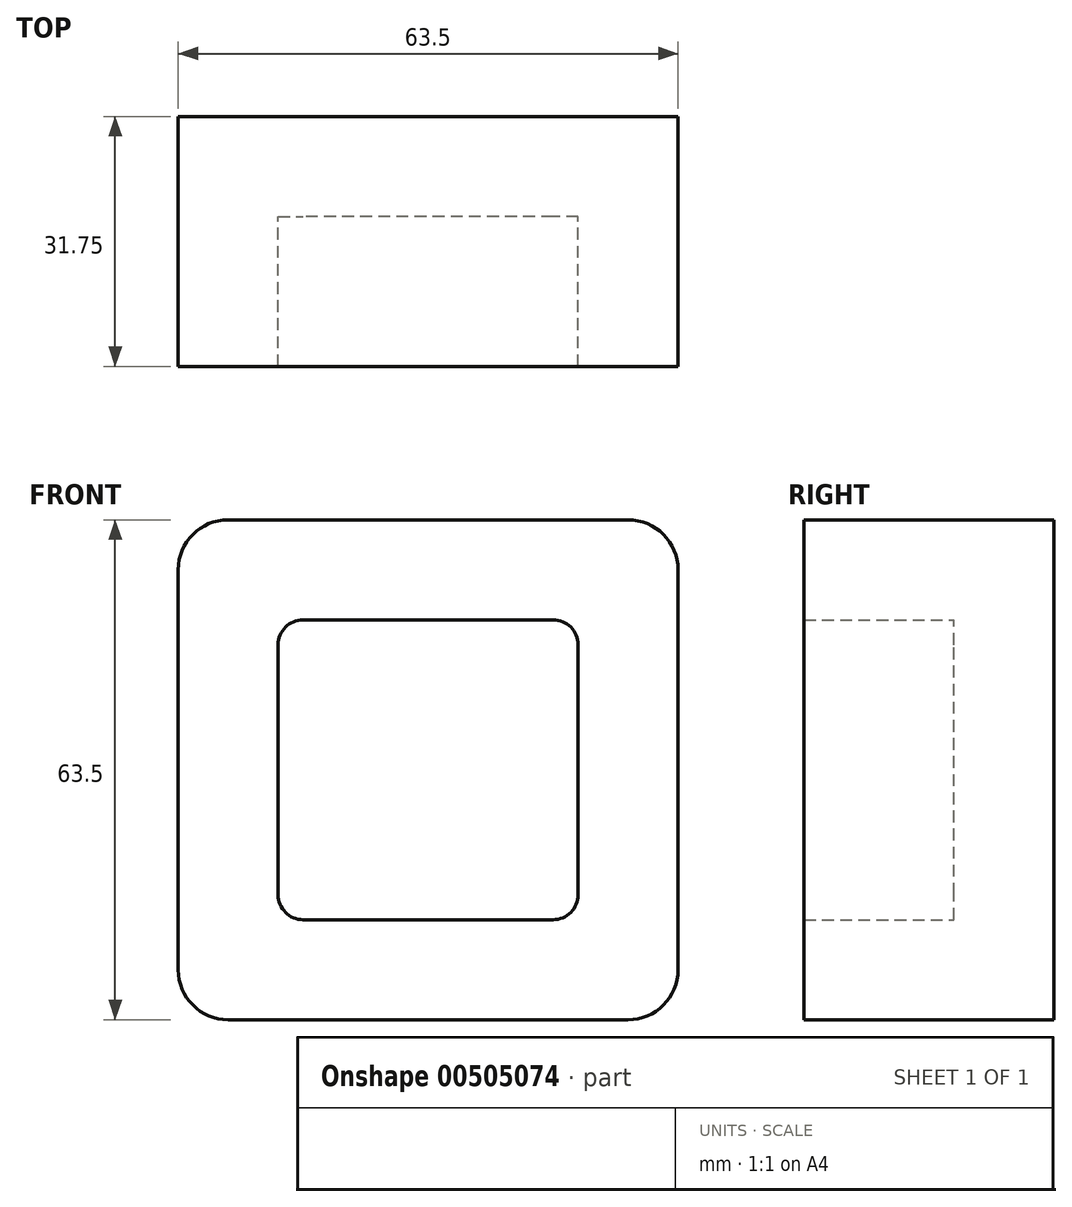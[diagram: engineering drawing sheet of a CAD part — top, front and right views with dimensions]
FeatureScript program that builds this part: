
annotation { "Feature Type Name" : "Feature", "Feature Type Description" : "" }
export const myFeature = defineFeature(function(context is Context, id is Id, definition is map)
    precondition{}
    {
        {
            var Q0;
            Q0=qCreatedBy(makeId("Front.planeOp"),FACE);
            var sketch = newSketch(context, id + "F0", { "sketchPlane" : qUnion([Q0])});
            skLineSegment(sketch, "E0.bottom", {"start": v(25.4, -31.75) * mm, "end": v(-25.4, -31.75) * mm});
            skLineSegment(sketch, "E0.top", {"start": v(25.4, 31.75) * mm, "end": v(-25.4, 31.75) * mm});
            skLineSegment(sketch, "E0.left", {"start": v(31.75, -25.4) * mm, "end": v(31.75, 25.4) * mm});
            skLineSegment(sketch, "E0.right", {"start": v(-31.75, -25.4) * mm, "end": v(-31.75, 25.4) * mm});
            skPoint(sketch, "E0.middle", {"position": v(0, 0) * mm});
            skPoint(sketch, "E1.visualSharp", {"position": v(-31.75, 31.75) * mm});
            skArc(sketch, "E1.filletArc", {"start": v(-25.4, 31.75) * mm, "mid": v(-29.9, 29.9) * mm, "end": v(-31.75, 25.4) * mm});
            skPoint(sketch, "E2.visualSharp", {"position": v(31.75, 31.75) * mm});
            skArc(sketch, "E2.filletArc", {"start": v(31.75, 25.4) * mm, "mid": v(29.9, 29.9) * mm, "end": v(25.4, 31.75) * mm});
            skPoint(sketch, "E3.visualSharp", {"position": v(31.75, -31.75) * mm});
            skArc(sketch, "E3.filletArc", {"start": v(25.4, -31.75) * mm, "mid": v(29.9, -29.9) * mm, "end": v(31.75, -25.4) * mm});
            skPoint(sketch, "E4.visualSharp", {"position": v(-31.75, -31.75) * mm});
            skArc(sketch, "E4.filletArc", {"start": v(-31.75, -25.4) * mm, "mid": v(-29.9, -29.9) * mm, "end": v(-25.4, -31.75) * mm});
            skLineSegment(sketch, "E5.0", {"start": v(-19.05, -15.87) * mm, "end": v(-19.05, 15.88) * mm});
            skLineSegment(sketch, "E5.1", {"start": v(15.87, -19.05) * mm, "end": v(-15.88, -19.05) * mm});
            skLineSegment(sketch, "E5.2", {"start": v(19.05, -15.87) * mm, "end": v(19.05, 15.88) * mm});
            skLineSegment(sketch, "E5.3", {"start": v(15.87, 19.05) * mm, "end": v(-15.88, 19.05) * mm});
            skPoint(sketch, "E6.visualSharp", {"position": v(-19.05, 19.05) * mm});
            skArc(sketch, "E6.filletArc", {"start": v(-15.88, 19.05) * mm, "mid": v(-18.12, 18.12) * mm, "end": v(-19.05, 15.88) * mm});
            skPoint(sketch, "E7.visualSharp", {"position": v(19.05, 19.05) * mm});
            skArc(sketch, "E7.filletArc", {"start": v(19.05, 15.88) * mm, "mid": v(18.12, 18.12) * mm, "end": v(15.87, 19.05) * mm});
            skPoint(sketch, "E8.visualSharp", {"position": v(19.05, -19.05) * mm});
            skArc(sketch, "E8.filletArc", {"start": v(15.87, -19.05) * mm, "mid": v(18.12, -18.12) * mm, "end": v(19.05, -15.87) * mm});
            skPoint(sketch, "E9.visualSharp", {"position": v(-19.05, -19.05) * mm});
            skArc(sketch, "E9.filletArc", {"start": v(-19.05, -15.87) * mm, "mid": v(-18.12, -18.12) * mm, "end": v(-15.88, -19.05) * mm});
            skSolve(sketch);
        }
        {
            var Q0;
            Q0=makeQuery(id+"F0.imprint","IMPRINT",FACE,{"disambiguationData":[TD([[makeQuery(id+"F0.imprint","IMPRINT",EDGE,{"derivedFrom":sQuery(id+"F0.wireOp",EDGE,"E5.0")}),-1.0]])]});
            extrude(context, id + "F1", {"entities" : qUnion([Q0]), "depth" : 12.7 * mm});
        }
        {
            var Q0;
            Q0=makeQuery(id+"F0.imprint","IMPRINT",FACE,{"disambiguationData":[TD([[makeQuery(id+"F0.imprint","IMPRINT",EDGE,{"derivedFrom":sQuery(id+"F0.wireOp",EDGE,"E0.bottom")}),-1.0]])]});
            extrude(context, id + "F2", {"entities" : qUnion([Q0]), "operationType" : NewBodyOperationType.ADD, "depth" : 31.75 * mm});
        }
    });
